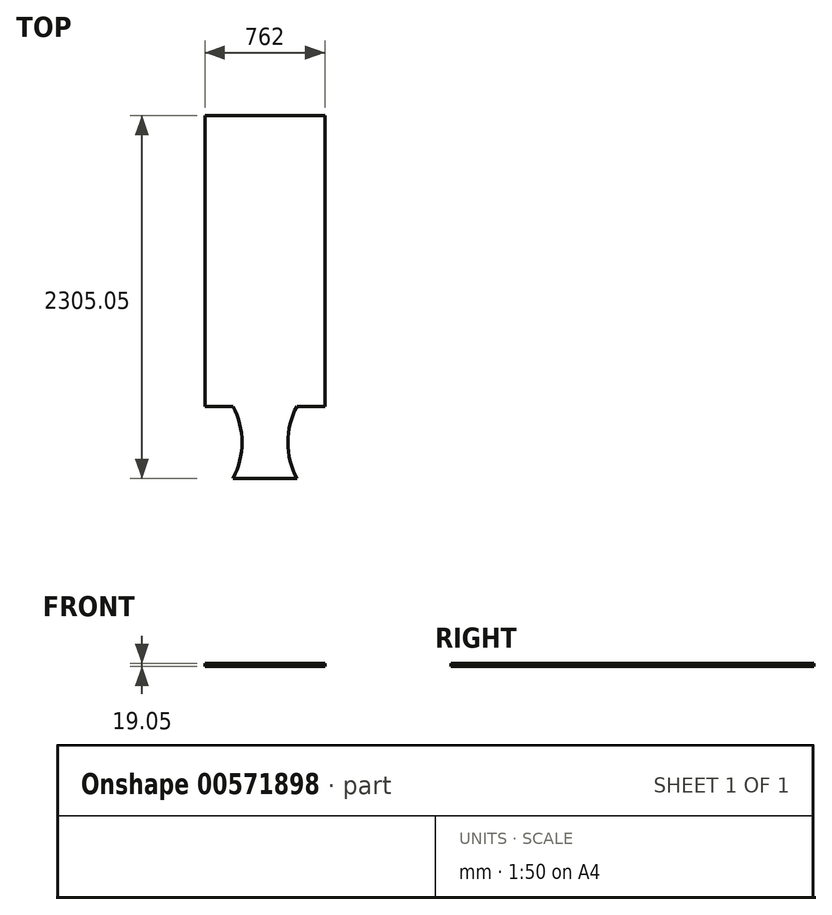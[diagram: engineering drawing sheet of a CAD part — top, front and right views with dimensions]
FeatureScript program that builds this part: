
annotation { "Feature Type Name" : "Feature", "Feature Type Description" : "" }
export const myFeature = defineFeature(function(context is Context, id is Id, definition is map)
    precondition{}
    {
        {
            var Q0;
            Q0=qCreatedBy(makeId("Top.planeOp"),FACE);
            var sketch = newSketch(context, id + "F0", { "sketchPlane" : qUnion([Q0])});
            skLineSegment(sketch, "E0.top", {"start": v(-208.69, -1920.55) * mm, "end": v(197.71, -1920.55) * mm});
            skArc(sketch, "E1", {"start": v(-208.69, -1920.55) * mm, "mid": v(-151.1, -1691.95) * mm, "end": v(-208.69, -1463.35) * mm});
            skArc(sketch, "E2", {"start": v(197.71, -1463.35) * mm, "mid": v(140.14, -1691.95) * mm, "end": v(197.71, -1920.55) * mm});
            skPoint(sketch, "E3.orphan", {"position": v(-386.49, -1920.55) * mm});
            skLineSegment(sketch, "E4", {"start": v(-386.49, -1463.35) * mm, "end": v(-208.69, -1463.35) * mm});
            skLineSegment(sketch, "E5", {"start": v(197.71, -1463.35) * mm, "end": v(375.51, -1463.35) * mm});
            skLineSegment(sketch, "E6", {"start": v(-386.49, 384.5) * mm, "end": v(375.51, 384.5) * mm, "construction": true});
            skLineSegment(sketch, "E7", {"start": v(-386.49, 384.5) * mm, "end": v(375.51, 384.5) * mm});
            skLineSegment(sketch, "E8", {"start": v(375.51, -1463.35) * mm, "end": v(197.71, -1463.35) * mm});
            skLineSegment(sketch, "E9", {"start": v(-386.49, 384.5) * mm, "end": v(-386.49, -1463.35) * mm});
            skLineSegment(sketch, "E10", {"start": v(375.51, 384.5) * mm, "end": v(375.51, -1463.35) * mm});
            skSolve(sketch);
        }
        {
            var Q0;
            Q0=makeQuery(id+"F0.imprint","IMPRINT",FACE,{"disambiguationData":[TD([[makeQuery(id+"F0.imprint","IMPRINT",EDGE,{"derivedFrom":sQuery(id+"F0.wireOp",EDGE,"E0.top")}),1.0]])]});
            extrude(context, id + "F1", {"entities" : qUnion([Q0]), "depth" : 19.05 * mm, "offsetDistance" : 25.4 * mm});
        }
    });
